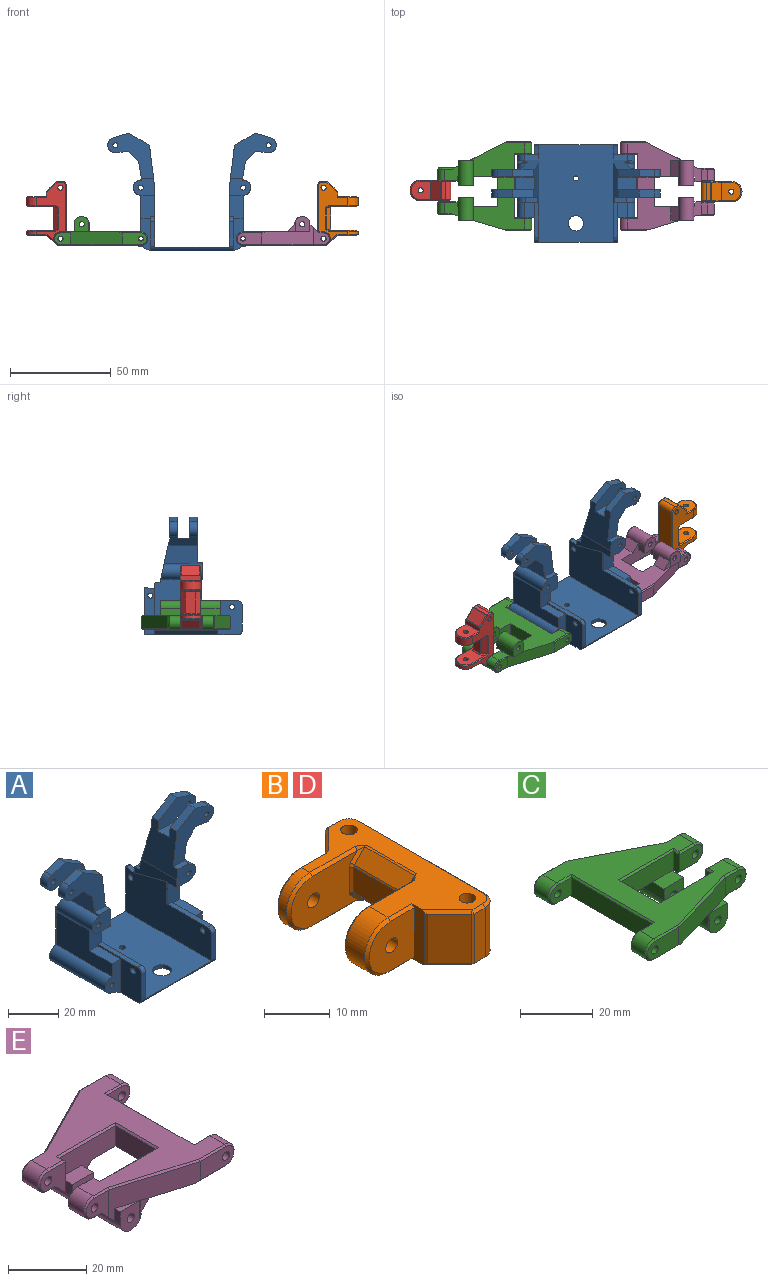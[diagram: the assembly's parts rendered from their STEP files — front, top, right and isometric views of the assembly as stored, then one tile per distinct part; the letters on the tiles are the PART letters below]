
ASSEMBLY  parts=5 mates=3
PART A: 99 faces, bbox 83.9x48.6x58.8 mm
  f0: plane 48.5x29.72mm, normal (1,0,0), area 1033.7mm2, adj f3,f8,f25,f49,f53,f54,f63,f64
  f1: plane 48.5x25.91mm, normal (-1,0,0), area 908.9mm2, adj f3,f10,f79,f80,f81,f82,f83,f84
  f2: plane 46.09x41.66mm, normal (0,0,-1), area 1868.2mm2, adj f4,f5,f6,f7,f9,f11,f12,f13
  f3: plane 48.42x37.06mm, normal (0,0,1), area 1743.5mm2, adj f0,f1,f93,f94,f95,f98
  f4: plane 23.6x4.81mm, normal (1,0,0), area 107.1mm2, adj f2,f10,f11,f13,f80,f85,f98
  f5: plane 23.6x4.81mm, normal (-1,0,0), area 107.1mm2, adj f2,f8,f9,f49,f91,f92,f98
  f6: plane 0.11x0mm, normal (-1,0,0), area 0mm2, adj f2,f9,f98
  f7: plane 0.11x0mm, normal (1,0,0), area 0mm2, adj f2,f11,f98
  f8: cylinder r=2.41mm len=2.26mm, axis (1,0,0), area 1mm2, adj f0,f5,f91,f98
  f9: cylinder r=2.41mm len=2.26mm, axis (1,0,0), area 0.2mm2, adj f2,f5,f6,f98
  f10: cylinder r=2.41mm len=2.29mm, axis (1,0,0), area 1mm2, adj f1,f4,f80,f98
  f11: cylinder r=2.41mm len=2.29mm, axis (1,0,0), area 0.2mm2, adj f2,f4,f7,f98
  f12: plane 16.25x8.41mm, normal (0,-1,0), area 87.7mm2, adj f2,f14,f35,f36,f37,f47,f86
  f13: plane 25.85x10.67mm, normal (0,1,0), area 138.3mm2, adj f2,f4,f35,f36,f37,f40,f47,f50
  f14: plane 12.58x4.6mm, normal (0,0,1), area 57.8mm2, adj f12,f37,f59,f86
  f15: plane 14.66x5.11mm, normal (0.71,0,-0.7), area 86.8mm2, adj f16,f17,f39,f51,f52,f56,f74,f75
  f16: plane 5.39x3.81mm, normal (-0.12,0,-0.99), area 20.7mm2, adj f15,f18,f51,f75
  f17: plane 5.39x3.81mm, normal (-0.12,0,-0.99), area 20.7mm2, adj f15,f19,f56,f76
  f18: cylinder r=3.81mm len=7.44mm, axis (0,1,0), area 45.7mm2, adj f16,f20,f51,f75
  f19: cylinder r=3.81mm len=7.44mm, axis (0,1,0), area 45.7mm2, adj f17,f21,f56,f76
  f20: plane 7.73x3.81mm, normal (0.3,0,0.95), area 30.9mm2, adj f18,f22,f51,f75
  f21: plane 7.73x3.81mm, normal (0.3,0,0.95), area 30.9mm2, adj f19,f23,f56,f76
  f22: plane 10.38x6.1mm, normal (-0.51,0,0.86), area 45.8mm2, adj f20,f24,f51,f75
  f23: plane 10.38x6.1mm, normal (-0.51,0,0.86), area 45.8mm2, adj f21,f24,f56,f76
  f24: plane 21.08x20.02mm, normal (-0.99,0,0.12), area 308.3mm2, adj f22,f23,f40,f51,f52,f56,f57,f60
  f25: plane 21.08x20.02mm, normal (0.99,0,0.12), area 308.3mm2, adj f0,f26,f27,f54,f55,f61,f63,f66
  f26: plane 10.38x6.1mm, normal (0.51,0,0.86), area 45.8mm2, adj f25,f28,f55,f70
  f27: plane 10.38x6.1mm, normal (0.51,0,0.86), area 45.8mm2, adj f25,f29,f61,f69
  f28: plane 7.73x3.81mm, normal (-0.3,0,0.95), area 30.9mm2, adj f26,f30,f55,f70
  f29: plane 7.73x3.81mm, normal (-0.3,0,0.95), area 30.9mm2, adj f27,f31,f61,f69
  f30: cylinder r=3.81mm len=7.44mm, axis (0,1,0), area 45.7mm2, adj f28,f32,f55,f70
  f31: cylinder r=3.81mm len=7.44mm, axis (0,1,0), area 45.7mm2, adj f29,f33,f61,f69
  f32: plane 5.39x3.81mm, normal (0.12,0,-0.99), area 20.7mm2, adj f30,f34,f55,f70
  f33: plane 5.39x3.81mm, normal (0.12,0,-0.99), area 20.7mm2, adj f31,f34,f61,f69
  f34: plane 14.66x5.11mm, normal (-0.71,0,-0.7), area 86.8mm2, adj f32,f33,f41,f54,f55,f61,f69,f70
  f35: plane 31.5x4.21mm, normal (0.48,0,-0.88), area 151.1mm2, adj f2,f12,f13,f36
  f36: cylinder r=3.81mm len=31.5mm, axis (0,1,0), area 388.5mm2, adj f12,f13,f35,f37
  f37: plane 31.5x17.78mm, normal (1,0,0), area 412.1mm2, adj f12,f13,f14,f36,f38,f50,f52,f57
  f38: cylinder r=3.81mm len=20.85mm, axis (0,1,0), area 246.6mm2, adj f37,f39,f52,f57
  f39: plane 19.2x9.22mm, normal (0.99,0,-0.16), area 148.9mm2, adj f15,f38,f52,f56,f57,f60
  f40: plane 23.99x14.48mm, normal (-1,0,0), area 124.8mm2, adj f13,f24,f50,f52,f57,f58,f59,f79
  f41: plane 19.2x9.22mm, normal (-0.99,0,-0.16), area 148.9mm2, adj f34,f42,f54,f61,f63,f66
  f42: cylinder r=3.81mm len=20.85mm, axis (0,1,0), area 246.6mm2, adj f41,f43,f54,f63
  f43: plane 31.5x17.78mm, normal (-1,0,0), area 412.1mm2, adj f42,f44,f48,f49,f53,f54,f62,f63
  f44: cylinder r=3.81mm len=31.5mm, axis (0,1,0), area 388.5mm2, adj f43,f46,f48,f49
  f45: cylinder r=1.14mm len=31.5mm, axis (0,1,0), area 226.2mm2, adj f48,f49
  f46: plane 31.5x4.21mm, normal (-0.48,0,-0.88), area 151.1mm2, adj f2,f44,f48,f49
  f47: cylinder r=1.14mm len=31.5mm, axis (0,1,0), area 226.2mm2, adj f12,f13
  f48: plane 16.25x8.41mm, normal (0,-1,0), area 87.7mm2, adj f2,f43,f44,f45,f46,f62,f89
  f49: plane 25.85x10.67mm, normal (0,1,0), area 138.3mm2, adj f0,f2,f5,f43,f44,f45,f46,f53
  f50: plane 6.86x2.81mm, normal (0,0.11,0.99), area 19.4mm2, adj f13,f37,f40,f52
  f51: plane 21.36x10.97mm, normal (0,1,0), area 155mm2, adj f15,f16,f18,f20,f22,f24,f52,f77
  f52: plane 21.66x11.23mm, normal (0,0.98,0.21), area 165.1mm2, adj f15,f24,f37,f38,f39,f40,f50,f51
  f53: plane 6.86x2.81mm, normal (0,0.11,0.99), area 19.4mm2, adj f0,f43,f49,f54
  f54: plane 21.66x11.23mm, normal (0,0.98,0.21), area 165.1mm2, adj f0,f25,f34,f41,f42,f43,f53,f55
  f55: plane 21.36x10.97mm, normal (0,1,0), area 155mm2, adj f25,f26,f28,f30,f32,f34,f54,f72
  f56: plane 22.77x22.38mm, normal (0,-1,0), area 230.8mm2, adj f15,f17,f19,f21,f23,f24,f39,f60
  f57: plane 10.67x8.81mm, normal (0,-1,0), area 76.4mm2, adj f24,f37,f38,f39,f40,f58,f60,f78
  f58: plane 6.86x5.07mm, normal (0,0,-1), area 34.8mm2, adj f37,f40,f57,f59
  f59: plane 11.24x6.86mm, normal (0,-1,0), area 75.4mm2, adj f14,f37,f40,f58,f82,f86
  f60: plane 6.06x2.54mm, normal (0,0,1), area 15.4mm2, adj f24,f39,f56,f57
  f61: plane 22.77x22.38mm, normal (0,-1,0), area 230.8mm2, adj f25,f27,f29,f31,f33,f34,f41,f66
  f62: plane 12.58x4.6mm, normal (0,0,1), area 57.8mm2, adj f43,f48,f65,f89
  f63: plane 10.67x8.81mm, normal (0,-1,0), area 76.4mm2, adj f0,f25,f41,f42,f43,f64,f66,f67
  f64: plane 6.86x5.07mm, normal (0,0,-1), area 34.8mm2, adj f0,f43,f63,f65
  f65: plane 11.24x6.86mm, normal (0,-1,0), area 75.4mm2, adj f0,f43,f62,f64,f89,f90
  f66: plane 6.06x2.54mm, normal (0,0,1), area 15.4mm2, adj f25,f41,f61,f63
  f67: cylinder r=1.27mm len=20.3mm, axis (0,1,0), area 159.8mm2, adj f54,f63
  f68: cylinder r=1.27mm len=3.81mm, axis (0,1,0), area 30.4mm2, adj f61,f69
  f69: plane 21.32x10.69mm, normal (0,1,0), area 152.4mm2, adj f25,f27,f29,f31,f33,f34,f68,f71
  f70: plane 21.32x10.69mm, normal (0,-1,0), area 152.4mm2, adj f25,f26,f28,f30,f32,f34,f71,f72
  f71: plane 9.34x6.35mm, normal (0,0,1), area 59.3mm2, adj f25,f34,f69,f70
  f72: cylinder r=1.27mm len=3.81mm, axis (0,1,0), area 30.4mm2, adj f55,f70
  f73: cylinder r=1.27mm len=3.81mm, axis (0,1,0), area 30.4mm2, adj f56,f76
  f74: plane 9.34x6.35mm, normal (0,0,1), area 59.3mm2, adj f15,f24,f75,f76
  f75: plane 21.32x10.69mm, normal (0,-1,0), area 152.4mm2, adj f15,f16,f18,f20,f22,f24,f74,f77
  f76: plane 21.32x10.69mm, normal (0,1,0), area 152.4mm2, adj f15,f17,f19,f21,f23,f24,f73,f74
  f77: cylinder r=1.27mm len=3.81mm, axis (0,1,0), area 30.4mm2, adj f51,f75
  f78: cylinder r=1.27mm len=20.3mm, axis (0,1,0), area 159.8mm2, adj f52,f57
  f79: plane 18.14x4.7mm, normal (0,0.25,0.97), area 0.5mm2, adj f1,f40,f80,f84
  f80: plane 4.38x2.29mm, normal (0,-0.14,0.99), area 10.1mm2, adj f1,f4,f10,f13,f79
  f81: plane 12.21x2.29mm, normal (0,-1,0), area 27.9mm2, adj f1,f86,f95,f97
  f82: plane 23.15x2.29mm, normal (0,0,1), area 51.1mm2, adj f1,f40,f59,f84,f86,f97
  f83: cylinder r=1.27mm len=2.54mm, axis (-1,0,0), area 18.2mm2, adj f1,f86
  f84: plane 10.67x0.03mm, normal (0,-1,0), area 0.3mm2, adj f1,f40,f79,f82
  f85: cylinder r=1.27mm len=2.54mm, axis (-1,0,0), area 18.2mm2, adj f1,f4
  f86: plane 24.77x17.02mm, normal (1,0,0), area 209.7mm2, adj f2,f12,f14,f59,f81,f82,f83,f95
  f87: cylinder r=1.27mm len=2.54mm, axis (-1,0,0), area 18mm2, adj f0,f89
  f88: plane 12.21x2.26mm, normal (0,-1,0), area 27.6mm2, adj f0,f89,f95,f96
  f89: plane 24.77x17.02mm, normal (-1,0,0), area 209.7mm2, adj f2,f48,f62,f65,f87,f88,f90,f95
  f90: plane 22.36x2.26mm, normal (0,0,1), area 50.6mm2, adj f0,f65,f89,f96
  f91: plane 4.38x2.26mm, normal (0,-0.14,0.99), area 10mm2, adj f0,f5,f8,f49
  f92: cylinder r=1.27mm len=2.54mm, axis (-1,0,0), area 18mm2, adj f0,f5
  f93: cylinder r=3.81mm len=7.62mm, axis (0,0,-1), area 42.6mm2, adj f2,f3
  f94: cylinder r=1.27mm len=2.54mm, axis (0,0,-1), area 14.2mm2, adj f2,f3
  f95: cylinder r=2.41mm len=41.61mm, axis (1,0,0), area 133.7mm2, adj f0,f1,f2,f3,f81,f86,f88,f89
  f96: cylinder r=2.41mm len=2.41mm, axis (1,0,0), area 8.5mm2, adj f0,f88,f89,f90
  f97: cylinder r=2.41mm len=2.41mm, axis (1,0,0), area 8.6mm2, adj f1,f81,f82,f86
  f98: plane 41.61x23.6mm, normal (0,1,0), area 173.2mm2, adj f0,f1,f2,f3,f4,f5,f6,f7
PART B: 77 faces, bbox 20.3x31.8x10.2 mm
  f0: plane 9.14x2.33mm, normal (0,-1,0), area 21.3mm2, adj f14,f62,f68,f73
  f1: plane 26.67x9.14mm, normal (1,0,0), area 243.9mm2, adj f13,f14,f57,f70
  f2: plane 9.14x2.33mm, normal (0,1,0), area 21.3mm2, adj f13,f53,f59,f64
  f3: plane 9.95x9.14mm, normal (0,1,0), area 76.9mm2, adj f20,f47,f48,f50,f51
  f4: plane 14.27x9.14mm, normal (0,-1,0), area 103.2mm2, adj f20,f30,f35,f36,f39,f40,f44,f45
  f5: plane 10.67x4.66mm, normal (-1,0,0), area 49.7mm2, adj f23,f29,f30,f31
  f6: plane 14.27x9.14mm, normal (0,1,0), area 103.2mm2, adj f19,f23,f24,f25,f26,f27,f28,f32
  f7: plane 9.65x9.14mm, normal (0,-1,0), area 74.2mm2, adj f9,f19,f74,f75,f76
  f8: cylinder r=1.27mm len=10.16mm, axis (0,0,-1), area 81.1mm2, adj f11,f12
  f9: plane 10.16x2.84mm, normal (-1,0,0), area 23.7mm2, adj f7,f11,f12,f63,f66,f69,f74,f76
  f10: cylinder r=1.27mm len=10.16mm, axis (0,0,-1), area 81.1mm2, adj f11,f12
  f11: plane 30.73x14.73mm, normal (0,0,1), area 211.3mm2, adj f8,f9,f10,f21,f22,f27,f34,f38
  f12: plane 30.73x14.73mm, normal (0,0,-1), area 211.3mm2, adj f8,f9,f10,f21,f22,f33,f37,f41
  f13: cylinder r=2.54mm len=9.14mm, axis (0,0,-1), area 36.5mm2, adj f1,f2,f54,f67
  f14: cylinder r=2.54mm len=9.14mm, axis (0,0,-1), area 36.5mm2, adj f0,f1,f60,f72
  f15: plane 9.14x4.78mm, normal (-0.71,-0.71,0), area 61.8mm2, adj f63,f66,f68,f69
  f16: plane 9.14x4.27mm, normal (-0.71,0.71,0), area 55.3mm2, adj f51,f52,f58,f59
  f17: plane 10.67x2.24mm, normal (-0.71,0,-0.71), area 33.8mm2, adj f31,f32,f40,f41
  f18: plane 10.67x2.24mm, normal (-0.71,0,0.71), area 33.8mm2, adj f28,f29,f38,f39
  f19: cylinder r=1.27mm len=5.08mm, axis (0,1,0), area 40.5mm2, adj f6,f7
  f20: cylinder r=1.27mm len=2.79mm, axis (0,1,0), area 22.3mm2, adj f3,f4
  f21: cylinder r=5.08mm len=10.16mm, axis (0,1,0), area 64.9mm2, adj f11,f12,f26,f75
  f22: cylinder r=5.08mm len=10.16mm, axis (0,1,0), area 28.4mm2, adj f11,f12,f46,f48
  f23: plane 4.66x0.51mm, normal (-0.71,0.71,0), area 3.3mm2, adj f5,f6,f24,f25
  f24: plane 0.72x0.66mm, normal (-0.68,0.68,0.28), area 0.4mm2, adj f6,f23,f28,f29
  f25: plane 0.72x0.66mm, normal (-0.68,0.68,-0.28), area 0.4mm2, adj f6,f23,f31,f32
  f26: cone r=4.57mm half-angle=45deg, axis (0,-1,0), area 10.9mm2, adj f6,f21,f27,f33
  f27: plane 9.7x0.51mm, normal (0,0.71,0.71), area 7mm2, adj f6,f11,f26,f34
  f28: plane 2.6x2.24mm, normal (-0.5,0.71,0.5), area 1.9mm2, adj f6,f18,f24,f34
  f29: plane 10.67x0.36mm, normal (-0.92,0,0.38), area 4.1mm2, adj f5,f18,f24,f35
  f30: plane 4.66x0.51mm, normal (-0.71,-0.71,0), area 3.3mm2, adj f4,f5,f35,f36
  f31: plane 10.67x0.36mm, normal (-0.92,0,-0.38), area 4.1mm2, adj f5,f17,f25,f36
  f32: plane 2.6x2.24mm, normal (-0.5,0.71,-0.5), area 1.9mm2, adj f6,f17,f25,f37
  f33: plane 9.7x0.51mm, normal (0,0.71,-0.71), area 7mm2, adj f6,f12,f26,f37
  f34: bspline ~1.44x1.02mm, area 0.7mm2, adj f11,f27,f28,f38
  f35: plane 0.72x0.66mm, normal (-0.68,-0.68,0.28), area 0.4mm2, adj f4,f29,f30,f39
  f36: plane 0.72x0.66mm, normal (-0.68,-0.68,-0.28), area 0.4mm2, adj f4,f30,f31,f40
  f37: bspline ~1.44x1.02mm, area 0.7mm2, adj f12,f32,f33,f41
  f38: plane 10.67x0.36mm, normal (-0.38,0,0.92), area 4.1mm2, adj f11,f18,f34,f42
  f39: plane 2.6x2.24mm, normal (-0.5,-0.71,0.5), area 1.9mm2, adj f4,f18,f35,f42
  f40: plane 2.6x2.24mm, normal (-0.5,-0.71,-0.5), area 1.9mm2, adj f4,f17,f36,f43
  f41: plane 10.67x0.36mm, normal (-0.38,0,-0.92), area 4.1mm2, adj f12,f17,f37,f43
  f42: bspline ~1.44x1.02mm, area 0.7mm2, adj f11,f38,f39,f44
  f43: bspline ~1.44x1.02mm, area 0.7mm2, adj f12,f40,f41,f45
  f44: plane 9.7x0.51mm, normal (0,-0.71,0.71), area 7mm2, adj f4,f11,f42,f46
  f45: plane 9.7x0.51mm, normal (0,-0.71,-0.71), area 7mm2, adj f4,f12,f43,f46
  f46: cone r=4.57mm half-angle=45deg, axis (0,1,0), area 10.9mm2, adj f4,f22,f44,f45
  f47: plane 5.38x0.51mm, normal (0,0.71,-0.71), area 3.9mm2, adj f3,f12,f48,f49
  f48: cone r=4.57mm half-angle=45deg, axis (0,-1,0), area 10.9mm2, adj f3,f22,f47,f50
  f49: plane 0.72x0.66mm, normal (-0.28,0.68,-0.68), area 0.4mm2, adj f12,f47,f51,f52
  f50: plane 5.38x0.51mm, normal (0,0.71,0.71), area 3.9mm2, adj f3,f11,f48,f55
  f51: plane 9.14x0.36mm, normal (-0.38,0.92,0), area 3.6mm2, adj f3,f16,f49,f55
  f52: plane 4.63x4.63mm, normal (-0.5,0.5,-0.71), area 4.3mm2, adj f12,f16,f49,f56
  f53: plane 2.33x0.51mm, normal (0,0.71,-0.71), area 1.7mm2, adj f2,f12,f54,f56
  f54: cone r=2.03mm half-angle=45deg, axis (0,0,1), area 2.6mm2, adj f12,f13,f53,f57
  f55: plane 0.72x0.66mm, normal (-0.28,0.68,0.68), area 0.4mm2, adj f11,f50,f51,f58
  f56: plane 0.51x0.51mm, normal (-0.28,0.68,-0.68), area 0.1mm2, adj f52,f53,f59
  f57: plane 26.67x0.51mm, normal (0.71,0,-0.71), area 19.2mm2, adj f1,f12,f54,f60
  f58: plane 4.63x4.63mm, normal (-0.5,0.5,0.71), area 4.3mm2, adj f11,f16,f55,f61
  f59: plane 9.14x0.36mm, normal (-0.38,0.92,0), area 3.6mm2, adj f2,f16,f56,f61
  f60: cone r=2.03mm half-angle=45deg, axis (0,0,1), area 2.6mm2, adj f12,f14,f57,f62
  f61: plane 0.51x0.51mm, normal (-0.28,0.68,0.68), area 0.1mm2, adj f58,f59,f64
  f62: plane 2.33x0.51mm, normal (0,-0.71,-0.71), area 1.7mm2, adj f0,f12,f60,f65
  f63: plane 5.65x5.29mm, normal (-0.5,-0.5,-0.71), area 5.2mm2, adj f9,f12,f15,f65,f66
  f64: plane 2.33x0.51mm, normal (0,0.71,0.71), area 1.7mm2, adj f2,f11,f61,f67
  f65: plane 0.51x0.51mm, normal (-0.28,-0.68,-0.68), area 0.1mm2, adj f62,f63,f68
  f66: plane 9.44x0.36mm, normal (-0.92,-0.38,0), area 3.6mm2, adj f9,f15,f63,f69
  f67: cone r=2.03mm half-angle=45deg, axis (0,0,-1), area 2.6mm2, adj f11,f13,f64,f70
  f68: plane 9.14x0.36mm, normal (-0.38,-0.92,0), area 3.6mm2, adj f0,f15,f65,f71
  f69: plane 5.65x5.29mm, normal (-0.5,-0.5,0.71), area 5.2mm2, adj f9,f11,f15,f66,f71
  f70: plane 26.67x0.51mm, normal (0.71,0,0.71), area 19.2mm2, adj f1,f11,f67,f72
  f71: plane 0.51x0.51mm, normal (-0.28,-0.68,0.68), area 0.1mm2, adj f68,f69,f73
  f72: cone r=2.03mm half-angle=45deg, axis (0,0,-1), area 2.6mm2, adj f11,f14,f70,f73
  f73: plane 2.33x0.51mm, normal (0,-0.71,0.71), area 1.7mm2, adj f0,f11,f71,f72
  f74: plane 5.08x0.51mm, normal (0,-0.71,-0.71), area 3.6mm2, adj f7,f9,f12,f75
  f75: cone r=4.57mm half-angle=45deg, axis (0,1,0), area 10.9mm2, adj f7,f21,f74,f76
  f76: plane 5.08x0.51mm, normal (0,-0.71,0.71), area 3.6mm2, adj f7,f9,f11,f75
PART C: 78 faces, bbox 46.9x44.1x14.5 mm
  f0: plane 6.91x6.73mm, normal (0,0,-1), area 38.4mm2, adj f3,f4,f16,f23,f39,f46,f70
  f1: plane 6.73x6.57mm, normal (0,0,-1), area 38.3mm2, adj f6,f7,f10,f20,f31,f56,f63
  f2: plane 9.14x5.84mm, normal (0,-1,0), area 44.7mm2, adj f3,f26,f46,f47,f48
  f3: plane 6.35x2.29mm, normal (-1,0,0), area 14.4mm2, adj f0,f2,f4,f46,f49
  f4: plane 20.32x6.35mm, normal (0,-1,0), area 129mm2, adj f0,f3,f5,f19,f36,f50
  f5: plane 14.74x6.35mm, normal (1,0,0), area 93.6mm2, adj f4,f6,f19,f51
  f6: plane 20.32x6.35mm, normal (0,1,0), area 129mm2, adj f1,f5,f7,f19,f28,f52
  f7: plane 6.35x2.29mm, normal (-1,0,0), area 14.4mm2, adj f1,f6,f8,f53,f56
  f8: plane 9.14x5.84mm, normal (0,1,0), area 44.7mm2, adj f7,f27,f54,f55,f56
  f9: plane 8.05x5.84mm, normal (0,-1,0), area 38.3mm2, adj f10,f27,f61,f62,f63
  f10: plane 27.31x12.06mm, normal (0.29,-0.96,0), area 169.8mm2, adj f1,f9,f11,f19,f33,f34,f35,f43
  f11: plane 12.19x5.84mm, normal (0,-1,0), area 62.5mm2, adj f10,f25,f57,f58,f59
  f12: plane 8.13x5.84mm, normal (0,1,0), area 38.8mm2, adj f13,f25,f75,f76,f77
  f13: plane 32.39x6.35mm, normal (-1,0,0), area 199.5mm2, adj f12,f14,f19,f71,f74,f77
  f14: plane 8.13x5.84mm, normal (0,-1,0), area 38.8mm2, adj f13,f24,f71,f72,f73
  f15: plane 12.19x5.84mm, normal (0,1,0), area 62.5mm2, adj f16,f24,f64,f65,f66
  f16: plane 26.6x13.59mm, normal (0.45,0.89,0), area 182.6mm2, adj f0,f15,f17,f19,f41,f64,f67,f70
  f17: plane 8.05x5.84mm, normal (0,1,0), area 38.3mm2, adj f16,f26,f68,f69,f70
  f18: plane 43.05x40.01mm, normal (0,0,1), area 763.8mm2, adj f20,f21,f22,f23,f48,f49,f50,f51
  f19: plane 43.05x27.27mm, normal (0,0,-1), area 664.3mm2, adj f4,f5,f6,f10,f13,f16,f21,f22
  f20: cylinder r=3.43mm len=6.86mm, axis (0,1,0), area 60.2mm2, adj f1,f18,f55,f62
  f21: cylinder r=3.43mm len=6.86mm, axis (0,-1,0), area 57.5mm2, adj f18,f19,f65,f72
  f22: cylinder r=3.43mm len=6.86mm, axis (0,-1,0), area 57.5mm2, adj f18,f19,f58,f76
  f23: cylinder r=3.43mm len=6.86mm, axis (0,1,0), area 60.2mm2, adj f0,f18,f47,f69
  f24: cylinder r=1.27mm len=6.35mm, axis (0,1,0), area 50.7mm2, adj f14,f15
  f25: cylinder r=1.27mm len=6.35mm, axis (0,1,0), area 50.7mm2, adj f11,f12
  f26: cylinder r=1.27mm len=6.6mm, axis (0,1,0), area 52.7mm2, adj f2,f17
  f27: cylinder r=1.27mm len=6.6mm, axis (0,1,0), area 52.7mm2, adj f8,f9
  f28: plane 7.62x4.52mm, normal (0,0,1), area 34.4mm2, adj f6,f29,f30,f31
  f29: plane 11.43x3.81mm, normal (-1,0,0), area 43.5mm2, adj f19,f28,f30,f34,f43
  f30: plane 7.62x7.62mm, normal (0,1,0), area 46.8mm2, adj f28,f29,f31,f43,f45
  f31: plane 11.43x3.81mm, normal (1,0,0), area 43.5mm2, adj f1,f28,f30,f32,f35,f43
  f32: plane 7.62x7.11mm, normal (0,-1,0), area 44.2mm2, adj f31,f33,f35,f43,f45
  f33: plane 5.71x0.01mm, normal (-1,0,0), area 0.1mm2, adj f10,f32,f35,f43
  f34: plane 5.65x0.47mm, normal (0,-1,0), area 2.4mm2, adj f10,f19,f29,f43
  f35: plane 7.11x2.13mm, normal (0,0,1), area 7.6mm2, adj f10,f31,f32,f33
  f36: plane 7.62x4.5mm, normal (0,0,1), area 34.3mm2, adj f4,f37,f39,f40
  f37: plane 12.7x3.81mm, normal (-1,0,0), area 48.4mm2, adj f19,f36,f38,f40,f42
  f38: plane 7.62x7.62mm, normal (0,1,0), area 46.8mm2, adj f19,f37,f39,f41,f42,f44
  f39: plane 12.7x3.81mm, normal (1,0,0), area 48.4mm2, adj f0,f36,f38,f40,f41,f42
  f40: plane 7.62x7.62mm, normal (0,-1,0), area 46.8mm2, adj f36,f37,f39,f42,f44
  f41: plane 6.01x3.07mm, normal (0,0,1), area 9.2mm2, adj f16,f38,f39
  f42: cylinder r=3.81mm len=12.7mm, axis (0,1,0), area 152mm2, adj f37,f38,f39,f40
  f43: cylinder r=3.81mm len=11.43mm, axis (0,1,0), area 136.8mm2, adj f10,f29,f30,f31,f32,f33,f34
  f44: cylinder r=1.27mm len=12.7mm, axis (0,1,0), area 101.3mm2, adj f38,f40
  f45: cylinder r=1.27mm len=11.43mm, axis (0,1,0), area 91.2mm2, adj f30,f32
  f46: plane 6.22x0.51mm, normal (0,-0.71,-0.71), area 4.5mm2, adj f0,f2,f3,f47
  f47: cone r=3.43mm half-angle=45deg, axis (0,1,0), area 7.2mm2, adj f2,f23,f46,f48
  f48: plane 6.22x0.51mm, normal (0,-0.71,0.71), area 4.3mm2, adj f2,f18,f47,f49
  f49: plane 2.79x0.51mm, normal (-0.71,0,0.71), area 1.6mm2, adj f3,f18,f48,f50
  f50: plane 21.34x0.51mm, normal (0,-0.71,0.71), area 15mm2, adj f4,f18,f49,f51
  f51: plane 15.76x0.51mm, normal (0.71,0,0.71), area 11mm2, adj f5,f18,f50,f52
  f52: plane 21.34x0.51mm, normal (0,0.71,0.71), area 15mm2, adj f6,f18,f51,f53
  f53: plane 2.8x0.51mm, normal (-0.71,0,0.71), area 1.6mm2, adj f7,f18,f52,f54
  f54: plane 6.22x0.51mm, normal (0,0.71,0.71), area 4.3mm2, adj f8,f18,f53,f55
  f55: cone r=3.43mm half-angle=45deg, axis (0,-1,0), area 7.2mm2, adj f8,f20,f54,f56
  f56: plane 6.22x0.51mm, normal (0,0.71,-0.71), area 4.5mm2, adj f1,f7,f8,f55
  f57: plane 10.98x0.51mm, normal (0,-0.71,-0.71), area 7.3mm2, adj f10,f11,f19,f58
  f58: cone r=3.43mm half-angle=45deg, axis (0,1,0), area 7.2mm2, adj f11,f22,f57,f59
  f59: plane 9.27x0.51mm, normal (0,-0.71,0.71), area 6.6mm2, adj f11,f18,f58,f60
  f60: plane 25.68x8.13mm, normal (0.2,-0.68,0.71), area 19.2mm2, adj f10,f18,f59,f61
  f61: plane 5.2x0.51mm, normal (0,-0.71,0.71), area 3.7mm2, adj f9,f18,f60,f62
  f62: cone r=3.43mm half-angle=45deg, axis (0,1,0), area 7.2mm2, adj f9,f20,f61,f63
  f63: plane 5.13x0.51mm, normal (0,-0.71,-0.71), area 3.1mm2, adj f1,f9,f10,f62
  f64: plane 10.27x0.51mm, normal (0,0.71,-0.71), area 7mm2, adj f15,f16,f19,f65
  f65: cone r=3.43mm half-angle=45deg, axis (0,-1,0), area 7.2mm2, adj f15,f21,f64,f66
  f66: plane 9.27x0.51mm, normal (0,0.71,0.71), area 6.6mm2, adj f15,f18,f65,f67
  f67: plane 25.73x13.59mm, normal (0.32,0.63,0.71), area 20.7mm2, adj f16,f18,f66,f68
  f68: plane 5.25x0.51mm, normal (0,0.71,0.71), area 3.7mm2, adj f17,f18,f67,f69
  f69: cone r=3.43mm half-angle=45deg, axis (0,-1,0), area 7.2mm2, adj f17,f23,f68,f70
  f70: plane 5.13x0.51mm, normal (0,0.71,-0.71), area 3.3mm2, adj f0,f16,f17,f69
  f71: plane 5.21x0.51mm, normal (0,-0.71,-0.71), area 3.7mm2, adj f13,f14,f19,f72
  f72: cone r=3.43mm half-angle=45deg, axis (0,1,0), area 7.2mm2, adj f14,f21,f71,f73
  f73: plane 5.72x0.51mm, normal (0,-0.71,0.71), area 3.9mm2, adj f14,f18,f72,f74
  f74: plane 32.39x0.51mm, normal (-0.71,0,0.71), area 22.9mm2, adj f13,f18,f73,f75
  f75: plane 5.72x0.51mm, normal (0,0.71,0.71), area 3.9mm2, adj f12,f18,f74,f76
  f76: cone r=3.43mm half-angle=45deg, axis (0,-1,0), area 7.2mm2, adj f12,f22,f75,f77
  f77: plane 5.21x0.51mm, normal (0,0.71,-0.71), area 3.7mm2, adj f12,f13,f19,f76
PART D: same geometry as B
PART E: 84 faces, bbox 46.9x44.1x14.5 mm
  f0: plane 4.52x3.81mm, normal (-1,0,0), area 17.2mm2, adj f8,f30,f32,f45
  f1: plane 3.81x3.07mm, normal (-1,0,0), area 11.7mm2, adj f18,f40,f43,f44
  f2: plane 5.59x2.92mm, normal (0,0,-1), area 16.3mm2, adj f25,f48,f52,f76
  f3: plane 5.59x2.92mm, normal (0,0,-1), area 16.3mm2, adj f22,f50,f62,f69
  f4: plane 9.65x9.14mm, normal (0,-1,0), area 51.9mm2, adj f5,f28,f48,f52,f53,f54
  f5: plane 9.65x2.29mm, normal (1,0,0), area 22.1mm2, adj f4,f6,f48,f55
  f6: plane 20.32x10.16mm, normal (0,-1,0), area 138.1mm2, adj f5,f7,f21,f38,f39,f41,f48,f49
  f7: plane 14.74x6.35mm, normal (-1,0,0), area 93.6mm2, adj f6,f8,f21,f57
  f8: plane 20.32x10.16mm, normal (0,1,0), area 138.1mm2, adj f0,f7,f9,f21,f30,f31,f50,f51
  f9: plane 9.65x2.29mm, normal (1,0,0), area 22.1mm2, adj f8,f10,f50,f59
  f10: plane 9.65x9.14mm, normal (0,1,0), area 51.9mm2, adj f9,f29,f50,f60,f61,f62
  f11: plane 8.56x8.05mm, normal (0,-1,0), area 42mm2, adj f12,f29,f50,f67,f68,f69
  f12: plane 25.6x12.06mm, normal (-0.29,-0.96,0), area 174.4mm2, adj f11,f13,f21,f33,f35,f36,f37,f45
  f13: plane 12.19x5.84mm, normal (0,-1,0), area 62.5mm2, adj f12,f27,f63,f64,f65
  f14: plane 8.13x5.84mm, normal (0,1,0), area 38.8mm2, adj f15,f27,f81,f82,f83
  f15: plane 32.39x6.35mm, normal (1,0,0), area 199.5mm2, adj f14,f16,f21,f77,f80,f83
  f16: plane 8.13x5.84mm, normal (0,-1,0), area 38.8mm2, adj f15,f26,f77,f78,f79
  f17: plane 12.19x5.84mm, normal (0,1,0), area 62.5mm2, adj f18,f26,f70,f71,f72
  f18: plane 25.6x13.08mm, normal (-0.45,0.89,0), area 187.7mm2, adj f1,f17,f19,f21,f43,f48,f70,f73
  f19: plane 8.56x8.05mm, normal (0,1,0), area 42mm2, adj f18,f28,f48,f74,f75,f76
  f20: plane 43.05x40.01mm, normal (0,0,1), area 763.8mm2, adj f22,f23,f24,f25,f54,f55,f56,f57
  f21: plane 43.05x27.27mm, normal (0,0,-1), area 606.7mm2, adj f6,f7,f8,f12,f15,f18,f23,f24
  f22: cylinder r=3.43mm len=6.86mm, axis (0,1,0), area 60.2mm2, adj f3,f20,f61,f68
  f23: cylinder r=3.43mm len=6.86mm, axis (0,-1,0), area 57.5mm2, adj f20,f21,f71,f78
  f24: cylinder r=3.43mm len=6.86mm, axis (0,-1,0), area 57.5mm2, adj f20,f21,f64,f82
  f25: cylinder r=3.43mm len=6.86mm, axis (0,1,0), area 60.2mm2, adj f2,f20,f53,f75
  f26: cylinder r=1.27mm len=6.35mm, axis (0,1,0), area 50.7mm2, adj f16,f17
  f27: cylinder r=1.27mm len=6.35mm, axis (0,1,0), area 50.7mm2, adj f13,f14
  f28: cylinder r=1.27mm len=6.6mm, axis (0,1,0), area 52.7mm2, adj f4,f19
  f29: cylinder r=1.27mm len=6.6mm, axis (0,1,0), area 52.7mm2, adj f10,f11
  f30: plane 7.62x4.52mm, normal (0,0,1), area 34.4mm2, adj f0,f8,f31,f32
  f31: plane 4.52x3.81mm, normal (1,0,0), area 17.2mm2, adj f8,f30,f32,f45
  f32: plane 7.62x7.62mm, normal (0,1,0), area 46.8mm2, adj f0,f30,f31,f45,f47
  f33: plane 3.81x2.13mm, normal (-1,0,0), area 8.1mm2, adj f12,f34,f37,f45
  f34: plane 7.62x7.11mm, normal (0,-1,0), area 44.2mm2, adj f33,f35,f37,f45,f47
  f35: plane 5.71x0.01mm, normal (1,0,0), area 0.1mm2, adj f12,f34,f37,f45
  f36: plane 5.65x4.28mm, normal (0,-1,0), area 9.6mm2, adj f12,f21,f45,f51
  f37: plane 7.11x2.13mm, normal (0,0,1), area 7.6mm2, adj f12,f33,f34,f35
  f38: plane 7.62x4.5mm, normal (0,0,1), area 34.3mm2, adj f6,f39,f41,f42
  f39: plane 4.5x3.81mm, normal (1,0,0), area 17.1mm2, adj f6,f38,f42,f44
  f40: plane 11.43x7.62mm, normal (0,1,0), area 54mm2, adj f1,f21,f43,f44,f46,f49
  f41: plane 4.5x3.81mm, normal (-1,0,0), area 17.1mm2, adj f6,f38,f42,f44
  f42: plane 7.62x7.62mm, normal (0,-1,0), area 46.8mm2, adj f38,f39,f41,f44,f46
  f43: plane 6.01x3.07mm, normal (0,0,1), area 9.2mm2, adj f1,f18,f40
  f44: cylinder r=3.81mm len=12.7mm, axis (0,1,0), area 152mm2, adj f1,f39,f40,f41,f42,f48,f49
  f45: cylinder r=3.81mm len=11.43mm, axis (0,1,0), area 136.8mm2, adj f0,f12,f31,f32,f33,f34,f35,f36
  f46: cylinder r=1.27mm len=12.7mm, axis (0,1,0), area 101.3mm2, adj f40,f42
  f47: cylinder r=1.27mm len=11.43mm, axis (0,1,0), area 91.2mm2, adj f32,f34
  f48: plane 7.42x4.32mm, normal (-0.71,0,-0.71), area 35.2mm2, adj f2,f4,f5,f6,f18,f19,f44,f52
  f49: plane 8.2x3.81mm, normal (0.71,0,-0.71), area 44.2mm2, adj f6,f21,f40,f44
  f50: plane 7.08x4.32mm, normal (-0.71,0,-0.71), area 34.8mm2, adj f3,f8,f9,f10,f11,f12,f45,f62
  f51: plane 6.91x3.81mm, normal (0.71,0,-0.71), area 37.3mm2, adj f8,f21,f36,f45
  f52: plane 2.92x0.51mm, normal (0,-0.71,-0.71), area 1.9mm2, adj f2,f4,f48,f53
  f53: cone r=2.92mm half-angle=45deg, axis (0,1,0), area 7.2mm2, adj f4,f25,f52,f54
  f54: plane 6.22x0.51mm, normal (0,-0.71,0.71), area 4.3mm2, adj f4,f20,f53,f55
  f55: plane 2.79x0.51mm, normal (0.71,0,0.71), area 1.6mm2, adj f5,f20,f54,f56
  f56: plane 21.34x0.51mm, normal (0,-0.71,0.71), area 15mm2, adj f6,f20,f55,f57
  f57: plane 15.76x0.51mm, normal (-0.71,0,0.71), area 11mm2, adj f7,f20,f56,f58
  f58: plane 21.34x0.51mm, normal (0,0.71,0.71), area 15mm2, adj f8,f20,f57,f59
  f59: plane 2.8x0.51mm, normal (0.71,0,0.71), area 1.6mm2, adj f9,f20,f58,f60
  f60: plane 6.22x0.51mm, normal (0,0.71,0.71), area 4.3mm2, adj f10,f20,f59,f61
  f61: cone r=2.92mm half-angle=45deg, axis (0,-1,0), area 7.2mm2, adj f10,f22,f60,f62
  f62: plane 2.92x0.51mm, normal (0,0.71,-0.71), area 1.9mm2, adj f3,f10,f50,f61
  f63: plane 10.98x0.51mm, normal (0,-0.71,-0.71), area 7.3mm2, adj f12,f13,f21,f64
  f64: cone r=2.92mm half-angle=45deg, axis (0,1,0), area 7.2mm2, adj f13,f24,f63,f65
  f65: plane 9.27x0.51mm, normal (0,-0.71,0.71), area 6.6mm2, adj f13,f20,f64,f66
  f66: plane 25.68x8.13mm, normal (-0.2,-0.68,0.71), area 19.2mm2, adj f12,f20,f65,f67
  f67: plane 5.2x0.51mm, normal (0,-0.71,0.71), area 3.7mm2, adj f11,f20,f66,f68
  f68: cone r=2.92mm half-angle=45deg, axis (0,1,0), area 7.2mm2, adj f11,f22,f67,f69
  f69: plane 2.92x0.51mm, normal (0,-0.71,-0.71), area 1.9mm2, adj f3,f11,f50,f68
  f70: plane 10.27x0.51mm, normal (0,0.71,-0.71), area 7mm2, adj f17,f18,f21,f71
  f71: cone r=2.92mm half-angle=45deg, axis (0,-1,0), area 7.2mm2, adj f17,f23,f70,f72
  f72: plane 9.27x0.51mm, normal (0,0.71,0.71), area 6.6mm2, adj f17,f20,f71,f73
  f73: plane 25.73x13.59mm, normal (-0.32,0.63,0.71), area 20.7mm2, adj f18,f20,f72,f74
  f74: plane 5.25x0.51mm, normal (0,0.71,0.71), area 3.7mm2, adj f19,f20,f73,f75
  f75: cone r=2.92mm half-angle=45deg, axis (0,-1,0), area 7.2mm2, adj f19,f25,f74,f76
  f76: plane 2.92x0.51mm, normal (0,0.71,-0.71), area 1.9mm2, adj f2,f19,f48,f75
  f77: plane 5.21x0.51mm, normal (0,-0.71,-0.71), area 3.7mm2, adj f15,f16,f21,f78
  f78: cone r=2.92mm half-angle=45deg, axis (0,1,0), area 7.2mm2, adj f16,f23,f77,f79
  f79: plane 5.72x0.51mm, normal (0,-0.71,0.71), area 3.9mm2, adj f16,f20,f78,f80
  f80: plane 32.39x0.51mm, normal (0.71,0,0.71), area 22.9mm2, adj f15,f20,f79,f81
  f81: plane 5.72x0.51mm, normal (0,0.71,0.71), area 3.9mm2, adj f14,f20,f80,f82
  f82: cone r=2.92mm half-angle=45deg, axis (0,-1,0), area 7.2mm2, adj f14,f24,f81,f83
  f83: plane 5.21x0.51mm, normal (0,0.71,-0.71), area 3.7mm2, adj f14,f15,f21,f82
PLACE A t=(20.41,60.71,32.93)mm
PLACE B rot(axis=(0,-0.71,0.71),180deg) t=(61.82,47.24,67.6)mm
PLACE C rot(axis=(0,1,0),180deg) t=(-22.39,22.99,42.45)mm
PLACE D rot(axis=(-1,0,0),90deg) t=(-62.66,37.72,67.6)mm
PLACE E rot(axis=(0,1,0),180deg) t=(21.55,22.86,42.45)mm
MATE revolute C.f21 <-> A.f44  axis (0,1,0) through (-25.82,60.71,39.02)mm
MATE revolute E.f23 <-> A.f36  axis (0,1,0) through (24.98,29.21,39.02)mm
MATE revolute D.f8 <-> C.f20  axis (0,1,0) through (-65.82,47.88,39.02)mm
